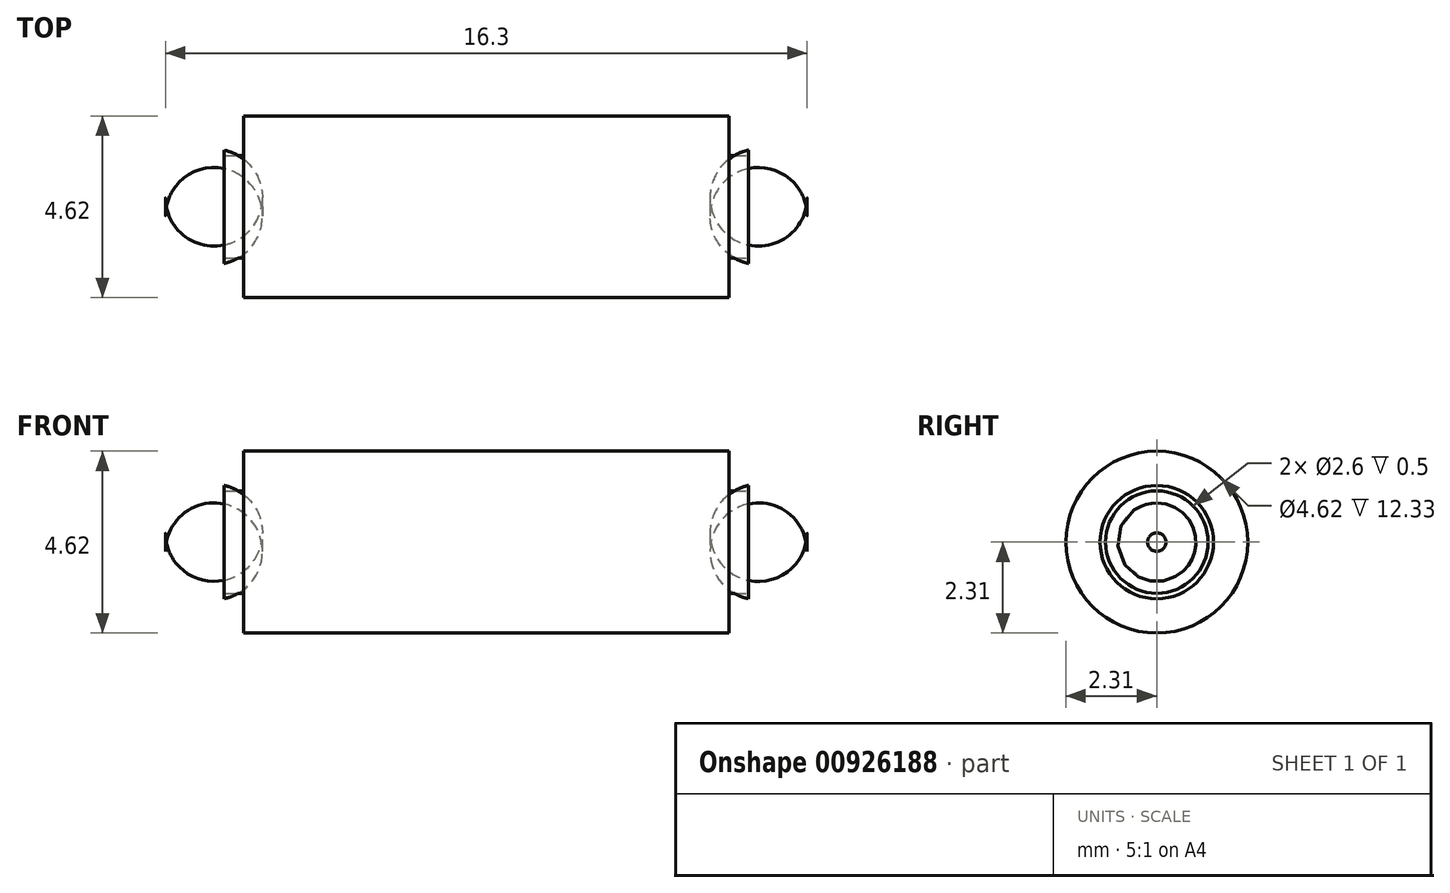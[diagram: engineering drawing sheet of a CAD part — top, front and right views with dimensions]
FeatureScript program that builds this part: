
annotation { "Feature Type Name" : "Feature", "Feature Type Description" : "" }
export const myFeature = defineFeature(function(context is Context, id is Id, definition is map)
    precondition{}
    {
        {
            var Q0;
            Q0=qCreatedBy(makeId("Front.planeOp"),FACE);
            var sketch = newSketch(context, id + "F0", { "sketchPlane" : qUnion([Q0])});
            skLineSegment(sketch, "E0", {"start": v(0, 2.31) * mm, "end": v(-6.17, 2.31) * mm});
            skLineSegment(sketch, "E1", {"start": v(-6.17, 2.3) * mm, "end": v(-6.17, 1.3) * mm});
            skLineSegment(sketch, "E2", {"start": v(-6.17, 1.3) * mm, "end": v(-6.67, 1.3) * mm});
            skLineSegment(sketch, "E3", {"start": v(-6.67, 1.3) * mm, "end": v(-6.67, 1.44) * mm});
            skLineSegment(sketch, "E4", {"start": v(-8.15, 0) * mm, "end": v(-8.15, 0.23) * mm});
            skArc(sketch, "E5", {"start": v(-6.67, 1.44) * mm, "mid": v(-7.7, 1.2) * mm, "end": v(-8.15, 0.23) * mm});
            skLineSegment(sketch, "E6", {"start": v(0, 3.94) * mm, "end": v(0, -3.56) * mm, "construction": true});
            skLineSegment(sketch, "E7.MirrorCS", {"start": v(8.15, 0) * mm, "end": v(8.15, 0.23) * mm});
            skArc(sketch, "E8.MirrorCS", {"start": v(6.67, 1.44) * mm, "mid": v(7.7, 1.2) * mm, "end": v(8.15, 0.23) * mm});
            skLineSegment(sketch, "E9.MirrorCS", {"start": v(6.67, 1.3) * mm, "end": v(6.67, 1.44) * mm});
            skLineSegment(sketch, "E10.MirrorCS", {"start": v(6.17, 1.3) * mm, "end": v(6.67, 1.3) * mm});
            skLineSegment(sketch, "E11.MirrorCS", {"start": v(6.17, 2.3) * mm, "end": v(6.17, 1.3) * mm});
            skLineSegment(sketch, "E12.MirrorCS", {"start": v(0, 2.31) * mm, "end": v(6.17, 2.31) * mm});
            skLineSegment(sketch, "E13", {"start": v(-10.73, 0) * mm, "end": v(10.4, 0) * mm, "construction": true});
            skSolve(sketch);
        }
        {
            var Q0;
            Q0=sQuery(id+"F0.wireOp",EDGE,"E0");
            var Q1;
            Q1=sQuery(id+"F0.wireOp",EDGE,"E1");
            var Q2;
            Q2=sQuery(id+"F0.wireOp",EDGE,"E2");
            var Q3;
            Q3=sQuery(id+"F0.wireOp",EDGE,"E12.MirrorCS");
            var Q4;
            Q4=sQuery(id+"F0.wireOp",EDGE,"E10.MirrorCS");
            var Q5;
            Q5=sQuery(id+"F0.wireOp",EDGE,"E8.MirrorCS");
            var Q6;
            Q6=sQuery(id+"F0.wireOp",EDGE,"E5");
            var Q7;
            Q7=sQuery(id+"F0.wireOp",EDGE,"E3");
            var Q8;
            Q8=sQuery(id+"F0.wireOp",EDGE,"E4");
            var Q9;
            Q9=sQuery(id+"F0.wireOp",EDGE,"E9.MirrorCS");
            var Q10;
            Q10=sQuery(id+"F0.wireOp",EDGE,"E7.MirrorCS");
            var Q11;
            Q11=sQuery(id+"F0.wireOp",EDGE,"E11.MirrorCS");
            var Q12;
            Q12=sQuery(id+"F0.wireOp",EDGE,"E13");
            revolve(context, id + "F1", {"bodyType" : ToolBodyType.SURFACE, "surfaceOperationType" : NewSurfaceOperationType.NEW, "surfaceEntities" : qUnion([Q0, Q1, Q2, Q3, Q4, Q5, Q6, Q7, Q8, Q9, Q10, Q11]), "axis" : qUnion([Q12]), "revolveType" : RevolveType.FULL});
        }
    });
